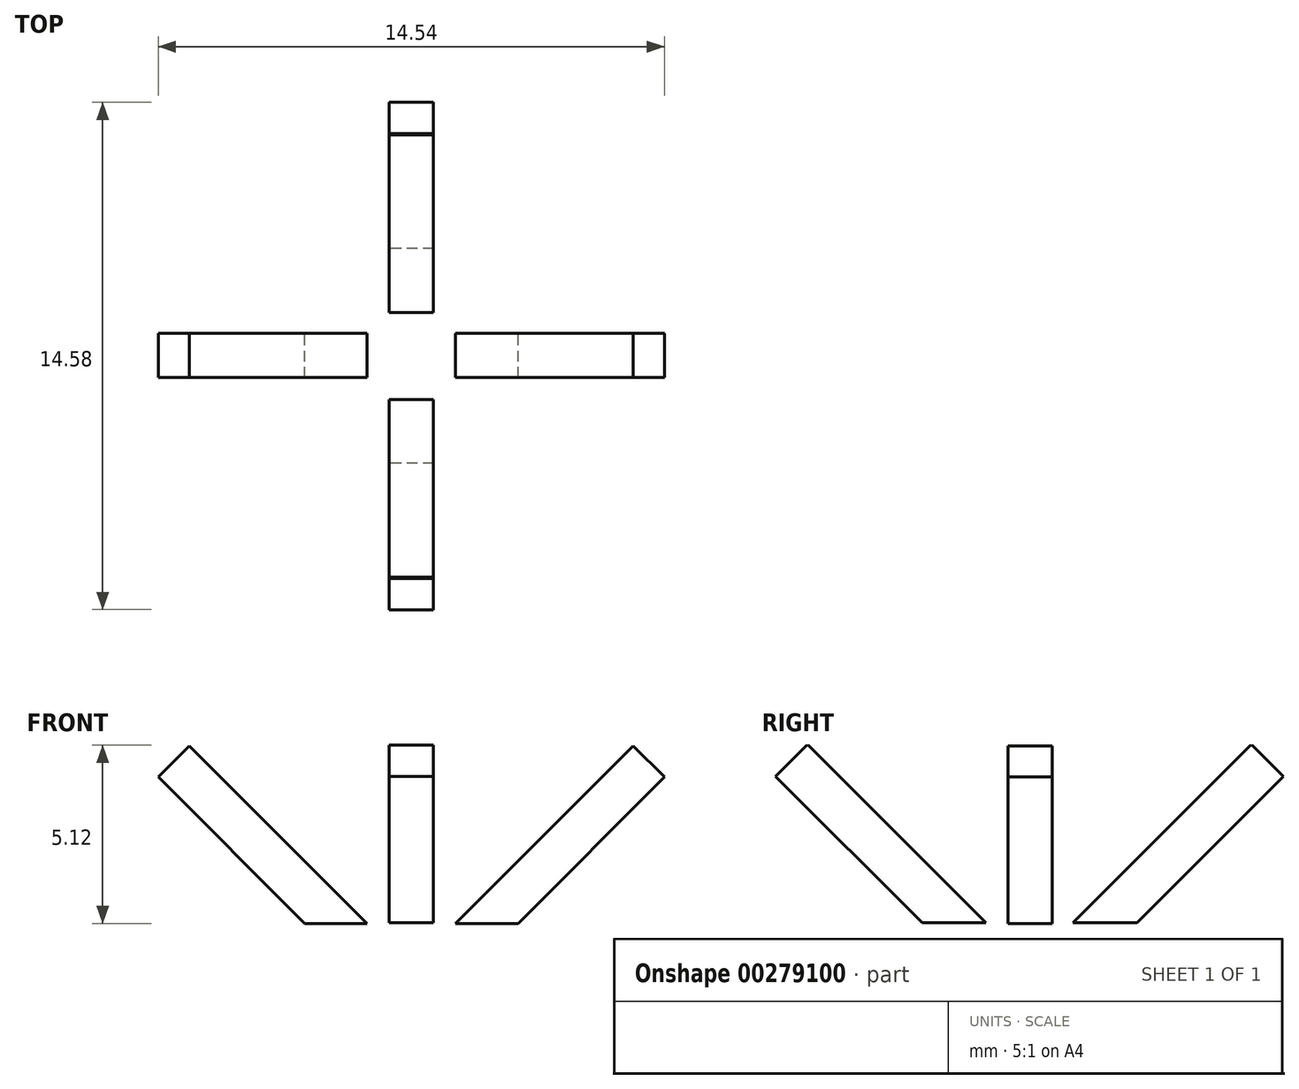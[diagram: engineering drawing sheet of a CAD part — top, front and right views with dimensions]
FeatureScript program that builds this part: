
annotation { "Feature Type Name" : "Feature", "Feature Type Description" : "" }
export const myFeature = defineFeature(function(context is Context, id is Id, definition is map)
    precondition{}
    {
        {
            var Q0;
            Q0=qCreatedBy(makeId("Front.planeOp"),FACE);
            var sketch = newSketch(context, id + "F0", { "sketchPlane" : qUnion([Q0])});
            skLineSegment(sketch, "E0", {"start": v(-1.27, 0) * mm, "end": v(-6.37, 5.1) * mm});
            skLineSegment(sketch, "E1", {"start": v(-6.37, 5.1) * mm, "end": v(-7.27, 4.2) * mm});
            skLineSegment(sketch, "E2", {"start": v(-7.27, 4.2) * mm, "end": v(-3.07, 0) * mm});
            skLineSegment(sketch, "E3", {"start": v(-3.07, 0) * mm, "end": v(-1.27, 0) * mm});
            skLineSegment(sketch, "E4.MirrorCS", {"start": v(6.37, 5.1) * mm, "end": v(7.27, 4.2) * mm});
            skLineSegment(sketch, "E5.MirrorCS", {"start": v(3.07, 0) * mm, "end": v(1.27, 0) * mm});
            skLineSegment(sketch, "E6.MirrorCS", {"start": v(1.27, 0) * mm, "end": v(6.37, 5.1) * mm});
            skLineSegment(sketch, "E7.MirrorCS", {"start": v(7.27, 4.2) * mm, "end": v(3.07, 0) * mm});
            skSolve(sketch);
        }
        {
            var Q0;
            Q0 = qSketchRegion(id + "F0", true);
            extrude(context, id + "F1", {"entities" : qUnion([Q0]), "endBound" : BoundingType.SYMMETRIC, "depth" : 1.27 * mm});
        }
        {
            var Q0;
            Q0=qCreatedBy(makeId("Right.planeOp"),FACE);
            var sketch = newSketch(context, id + "F2", { "sketchPlane" : qUnion([Q0])});
            skLineSegment(sketch, "E8", {"start": v(-1.31, 0.02) * mm, "end": v(-6.42, 5.12) * mm});
            skLineSegment(sketch, "E9", {"start": v(-6.42, 5.12) * mm, "end": v(-7.31, 4.22) * mm});
            skLineSegment(sketch, "E10", {"start": v(-7.31, 4.22) * mm, "end": v(-3.1, 0.02) * mm});
            skLineSegment(sketch, "E11", {"start": v(-3.1, 0.02) * mm, "end": v(-1.31, 0.02) * mm});
            skLineSegment(sketch, "E12.MirrorCS", {"start": v(6.33, 5.12) * mm, "end": v(7.23, 4.22) * mm});
            skLineSegment(sketch, "E13.MirrorCS", {"start": v(3.02, 0.02) * mm, "end": v(1.23, 0.02) * mm});
            skLineSegment(sketch, "E14.MirrorCS", {"start": v(1.23, 0.02) * mm, "end": v(6.33, 5.12) * mm});
            skLineSegment(sketch, "E15.MirrorCS", {"start": v(7.23, 4.22) * mm, "end": v(3.02, 0.02) * mm});
            skLineSegment(sketch, "E16.MirrorCS", {"start": v(1.27, 0.02) * mm, "end": v(6.37, 5.12) * mm});
            skLineSegment(sketch, "E17.MirrorCS", {"start": v(6.37, 5.12) * mm, "end": v(7.27, 4.22) * mm});
            skLineSegment(sketch, "E18.MirrorCS", {"start": v(7.27, 4.22) * mm, "end": v(3.07, 0.02) * mm});
            skLineSegment(sketch, "E19.MirrorCS", {"start": v(3.07, 0.02) * mm, "end": v(1.27, 0.02) * mm});
            skLineSegment(sketch, "E20.MirrorCS", {"start": v(-1.27, 0.02) * mm, "end": v(-6.37, 5.12) * mm});
            skLineSegment(sketch, "E21.MirrorCS", {"start": v(-3.07, 0.02) * mm, "end": v(-1.27, 0.02) * mm});
            skLineSegment(sketch, "E22.MirrorCS", {"start": v(-7.27, 4.22) * mm, "end": v(-3.07, 0.02) * mm});
            skLineSegment(sketch, "E23.MirrorCS", {"start": v(-6.37, 5.12) * mm, "end": v(-7.27, 4.22) * mm});
            skSolve(sketch);
        }
        {
            var Q0;
            Q0 = qSketchRegion(id + "F2", true);
            extrude(context, id + "F3", {"entities" : qUnion([Q0]), "endBound" : BoundingType.SYMMETRIC, "depth" : 1.27 * mm});
        }
    });
